FCSTD DOCUMENT  (FreeCAD 0.17R11939 (Git))
Label: bridgeport_motor_lock
License: All rights reserved
LicenseURL: http://en.wikipedia.org/wiki/All_rights_reserved
objects: Sketcher::SketchObject×1, PartDesign::Body×1
note: 2 computed .brp shape members not serialized (recipe doc carries the construction recipe); baked Part::Feature solids carry a one-line shape summary decoded from their .brp

FEATURE [Sketcher::SketchObject] Sketch
  MapMode = 5
  Support = -> [XY_Plane]
  sketch-geometry (11):
    g0: ArcOfCircle CenterX=0 CenterY=0 CenterZ=0 NormalX=0 NormalY=0 NormalZ=1 Radius=18.597 StartAngle=0.189332 EndAngle=6.09385
    g1: Circle CenterX=0 CenterY=0 CenterZ=0 NormalX=0 NormalY=0 NormalZ=1 Radius=4.7625
    g2: LineSegment StartX=18.2647 StartY=2.5 StartZ=0 EndX=8.26465 EndY=2.5 EndZ=0
    g3: LineSegment [constr] StartX=8.26465 StartY=2.5 StartZ=0 EndX=8.26465 EndY=-2.5 EndZ=0
    g4: LineSegment StartX=8.26465 StartY=-2.5 StartZ=0 EndX=18.2647 EndY=-2.5 EndZ=0
    g5: LineSegment StartX=18.2647 StartY=2.5 StartZ=0 EndX=18.2647 EndY=3.5 EndZ=0
    g6: LineSegment StartX=18.2647 StartY=-2.5 StartZ=0 EndX=18.2647 EndY=-3.5 EndZ=0
    g7: LineSegment [constr] StartX=18.2647 StartY=-2.5 StartZ=0 EndX=18.2647 EndY=2.5 EndZ=0
    g8: LineSegment StartX=8.26465 StartY=2.5 StartZ=0 EndX=6.7625 EndY=0 EndZ=0
    g9: LineSegment StartX=6.7625 StartY=0 StartZ=0 EndX=8.26465 EndY=-2.5 EndZ=0
    g10: LineSegment [constr] StartX=6.7625 StartY=0 StartZ=0 EndX=4.7625 EndY=0 EndZ=0
  constraints (30):
    c: Coincident(g0,g-1)
    c: Coincident(g1,g-1)
    c: Radius(g1) = 4.7625
    c: Horizontal(g2)
    c: Coincident(g3,g2)
    c: Coincident(g4,g3)
    c: Horizontal(g4)
    c: Vertical(g3)
    c: Coincident(g5,g2)
    c: Coincident(g5,g0)
    c: Vertical(g5)
    c: Coincident(g6,g4)
    c: Coincident(g6,g0)
    c: Vertical(g6)
    c: Coincident(g7,g4)
    c: Coincident(g7,g2)
    c: Vertical(g7)
    c: Equal(g5,g6)
    c: Distance(g3) = 5
    c: Distance(g2) = 10
    c: Distance(g0,g0) = 7
    c: Coincident(g8,g2)
    c: PointOnObject(g8,g-1)
    c: Coincident(g9,g8)
    c: Coincident(g9,g3)
    c: Angle(g9,g8) = 2.05949
    c: Coincident(g10,g8)
    c: PointOnObject(g10,g1)
    c: Horizontal(g10)
    c: Distance(g10) = 2
FEATURE [PartDesign::Body] Body
  Group = -> [Sketch]
  Origin = -> Origin
